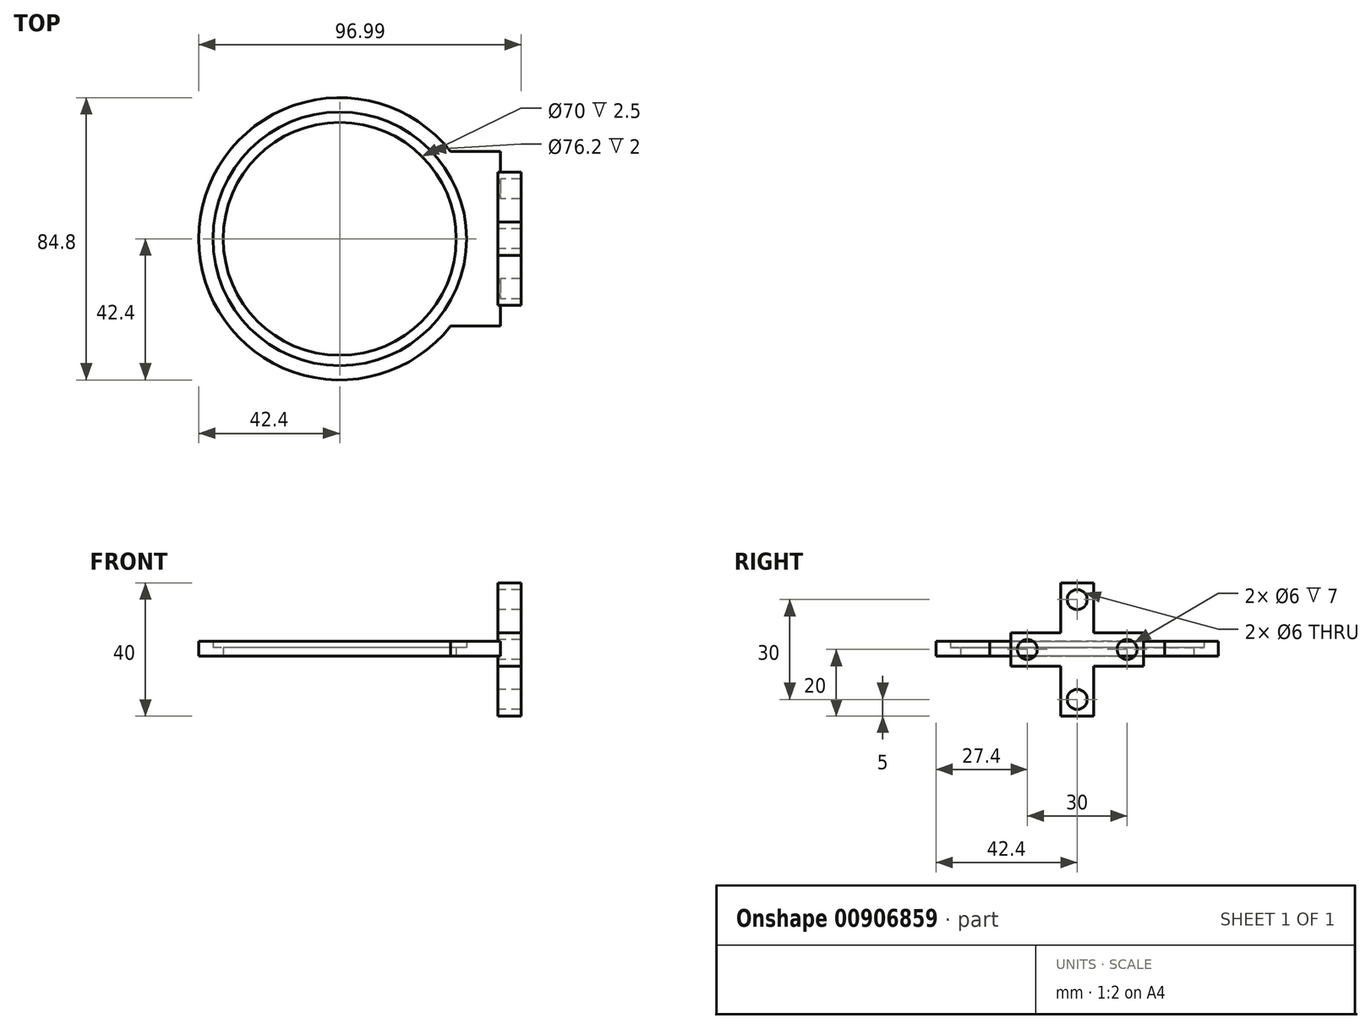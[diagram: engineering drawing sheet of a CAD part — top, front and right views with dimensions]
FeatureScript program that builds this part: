
annotation { "Feature Type Name" : "Feature", "Feature Type Description" : "" }
export const myFeature = defineFeature(function(context is Context, id is Id, definition is map)
    precondition{}
    {
        {
            var Q0;
            Q0=qCreatedBy(makeId("Top.planeOp"),FACE);
            var sketch = newSketch(context, id + "F0", { "sketchPlane" : qUnion([Q0])});
            skCircle(sketch, "E0", {"center": v(0, 0) * mm, "radius": 42.4 * mm});
            skCircle(sketch, "E1", {"center": v(0, 0) * mm, "radius": 35 * mm});
            skSolve(sketch);
        }
        {
            var Q0;
            Q0 = qSketchRegion(id + "F0", true);
            extrude(context, id + "F1", {"entities" : qUnion([Q0]), "depth" : 2.5 * mm, "offsetDistance" : 25 * mm});
        }
        {
            var Q0;
            Q0=makeQuery(id+"F1.opExtrude","CAP_FACE",FACE,{"disambiguationData":[OSD([sQuery(id+"F0.wireOp",EDGE,"E0"),sQuery(id+"F0.wireOp",EDGE,"E1")])],"isStart":false});
            var sketch = newSketch(context, id + "F2", { "sketchPlane" : qUnion([Q0])});
            skCircle(sketch, "E2", {"center": v(0, 0) * mm, "radius": 38.1 * mm});
            skCircle(sketch, "E3.0", {"center": v(0, 0) * mm, "radius": 42.4 * mm});
            skSolve(sketch);
        }
        {
            var Q0;
            Q0 = qSketchRegion(id + "F2", true);
            extrude(context, id + "F3", {"entities" : qUnion([Q0]), "operationType" : NewBodyOperationType.ADD, "depth" : 2 * mm, "offsetDistance" : 25 * mm});
        }
        {
            var Q0;
            Q0=qCreatedBy(makeId("Right.planeOp"),FACE);
            cPlane(context, id + "F4", {"entities" : qUnion([Q0]), "cplaneType" : CPlaneType.OFFSET, "offset" : 44.39 * mm, "width" : 150 * mm, "height" : 150 * mm});
        }
        {
            var Q0;
            Q0=qCreatedBy(id+"F4.planeOp",FACE);
            var sketch = newSketch(context, id + "F5", { "sketchPlane" : qUnion([Q0])});
            skLineSegment(sketch, "E4.bottom", {"start": v(20, 7) * mm, "end": v(5, 7) * mm});
            skLineSegment(sketch, "E4.top", {"start": v(20, -3) * mm, "end": v(5, -3) * mm});
            skLineSegment(sketch, "E4.left", {"start": v(20, 7) * mm, "end": v(20, -3) * mm});
            skLineSegment(sketch, "E4.right", {"start": v(-20, 7) * mm, "end": v(-20, -3) * mm});
            skPoint(sketch, "E4.middle", {"position": v(0, 2) * mm});
            skLineSegment(sketch, "E5.bottom", {"start": v(5, 22) * mm, "end": v(-5, 22) * mm});
            skLineSegment(sketch, "E5.top", {"start": v(5, -18) * mm, "end": v(-5, -18) * mm});
            skLineSegment(sketch, "E5.left", {"start": v(5, 22) * mm, "end": v(5, 7) * mm});
            skLineSegment(sketch, "E5.right", {"start": v(-5, 22) * mm, "end": v(-5, 7) * mm});
            skLineSegment(sketch, "E6.trimOffspring", {"start": v(5, -3) * mm, "end": v(5, -18) * mm});
            skLineSegment(sketch, "E7.trimOffspring", {"start": v(-5, 7) * mm, "end": v(-20, 7) * mm});
            skLineSegment(sketch, "E8.trimOffspring", {"start": v(-5, -3) * mm, "end": v(-5, -18) * mm});
            skLineSegment(sketch, "E9.trimOffspring", {"start": v(-5, -3) * mm, "end": v(-20, -3) * mm});
            skCircle(sketch, "E10", {"center": v(0, 17) * mm, "radius": 3 * mm});
            skCircle(sketch, "E11", {"center": v(0, -13) * mm, "radius": 3 * mm});
            skCircle(sketch, "E12", {"center": v(-15, 2) * mm, "radius": 3 * mm});
            skCircle(sketch, "E13", {"center": v(15, 2) * mm, "radius": 3 * mm});
            skSolve(sketch);
        }
        {
            var Q0;
            Q0=makeQuery(id+"F3.opExtrude","CAP_FACE",FACE,{"disambiguationData":[OSD([sQuery(id+"F2.wireOp",EDGE,"E2"),sQuery(id+"F2.wireOp",EDGE,"E3.0")])],"isStart":false});
            var sketch = newSketch(context, id + "F6", { "sketchPlane" : qUnion([Q0])});
            skLineSegment(sketch, "E14", {"start": v(48.3, 26.25) * mm, "end": v(48.3, -26.25) * mm});
            skArc(sketch, "E15.0", {"start": v(33.3, -26.25) * mm, "mid": v(42.4, 0) * mm, "end": v(33.3, 26.25) * mm});
            skLineSegment(sketch, "E16", {"start": v(48.3, 26.25) * mm, "end": v(33.3, 26.25) * mm});
            skLineSegment(sketch, "E17", {"start": v(48.3, -26.25) * mm, "end": v(33.3, -26.25) * mm});
            skSolve(sketch);
        }
        {
            var Q0;
            Q0 = qSketchRegion(id + "F6", true);
            extrude(context, id + "F7", {"entities" : qUnion([Q0]), "operationType" : NewBodyOperationType.ADD, "oppositeDirection" : true, "depth" : 4.5 * mm, "offsetDistance" : 25 * mm});
        }
        {
            var Q0;
            Q0 = qSketchRegion(id + "F5", true);
            extrude(context, id + "F8", {"entities" : qUnion([Q0]), "operationType" : NewBodyOperationType.ADD, "depth" : 10.2 * mm, "offsetDistance" : 25 * mm, "hasSecondDirection" : true, "secondDirectionOppositeDirection" : false, "secondDirectionDepth" : 3.2 * mm});
        }
    });
